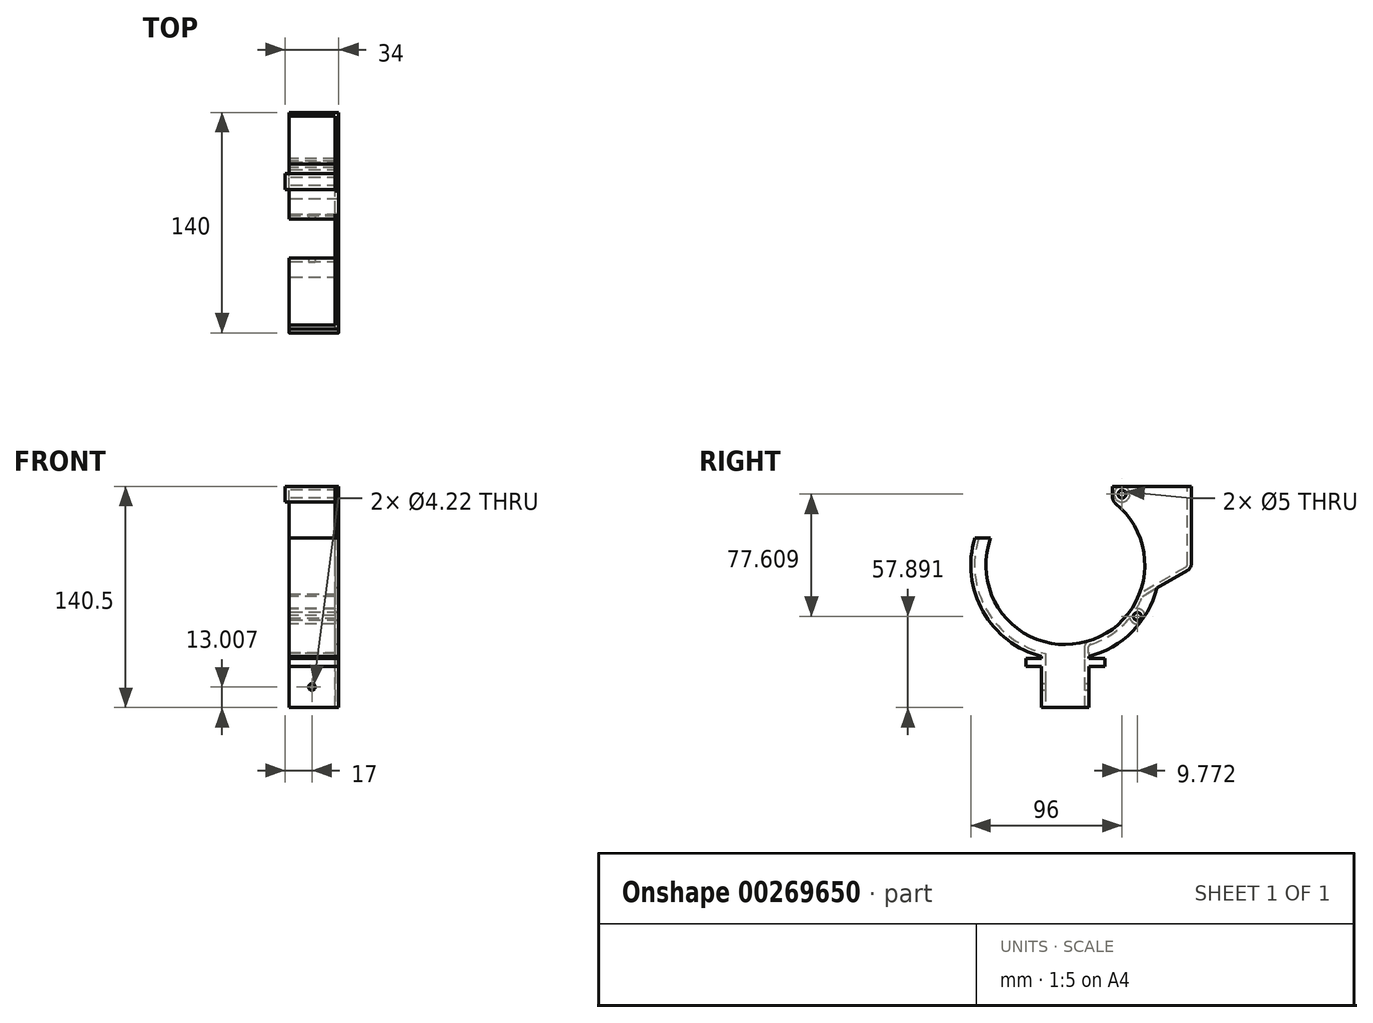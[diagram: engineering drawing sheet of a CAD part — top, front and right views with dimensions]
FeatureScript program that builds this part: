
annotation { "Feature Type Name" : "Feature", "Feature Type Description" : "" }
export const myFeature = defineFeature(function(context is Context, id is Id, definition is map)
    precondition{}
    {
        {
            var Q0;
            Q0=qCreatedBy(makeId("Right.planeOp"),FACE);
            var sketch = newSketch(context, id + "F0", { "sketchPlane" : qUnion([Q0])});
            skLineSegment(sketch, "E0", {"start": v(50, -52.08) * mm, "end": v(50, 0) * mm});
            skLineSegment(sketch, "E1", {"start": v(50, 0) * mm, "end": v(0, 0) * mm});
            skArc(sketch, "E2", {"start": v(-77.52, -32.91) * mm, "mid": v(-15.33, -98.32) * mm, "end": v(0, -9.38) * mm});
            skLineSegment(sketch, "E3", {"start": v(0, 0) * mm, "end": v(0, -9.38) * mm});
            skLineSegment(sketch, "E4", {"start": v(50, -52.08) * mm, "end": v(28.18, -64.68) * mm});
            skCircle(sketch, "E5", {"center": v(-30, -50) * mm, "radius": 50.5 * mm, "construction": true});
            skLineSegment(sketch, "E6", {"start": v(-77.52, -32.91) * mm, "end": v(-87.52, -32.91) * mm});
            skLineSegment(sketch, "E7", {"start": v(-15, -140.5) * mm, "end": v(-15, -108.1) * mm});
            skLineSegment(sketch, "E8", {"start": v(-45, -108.1) * mm, "end": v(-45, -140.5) * mm});
            skLineSegment(sketch, "E9", {"start": v(-45, -140.5) * mm, "end": v(-15, -140.5) * mm});
            skArc(sketch, "E10", {"start": v(-15, -108.1) * mm, "mid": v(12.54, -92.3) * mm, "end": v(28.18, -64.68) * mm});
            skArc(sketch, "E11.trimOffspring", {"start": v(-87.52, -32.91) * mm, "mid": v(-82.23, -79.54) * mm, "end": v(-45, -108.1) * mm});
            skLineSegment(sketch, "E12", {"start": v(-30, -50) * mm, "end": v(-30, -129.79) * mm, "construction": true});
            skSolve(sketch);
        }
        {
            var Q0;
            Q0 = qSketchRegion(id + "F0", true);
            extrude(context, id + "F1", {"entities" : qUnion([Q0]), "depth" : 34 * mm});
        }
        {
            var Q0;
            Q0=makeQuery(id+"F1.opExtrude","SWEPT_EDGE",EDGE,{"disambiguationData":[OSD([sQuery(id+"F0.wireOp",EDGE,"E0"),sQuery(id+"F0.wireOp",EDGE,"E4")])]});
            var Q1;
            Q1=makeQuery(id+"F1.opExtrude","SWEPT_EDGE",EDGE,{"disambiguationData":[OSD([sQuery(id+"F0.wireOp",EDGE,"E2"),sQuery(id+"F0.wireOp",EDGE,"E3")])]});
            fillet(context, id + "F2", {"entities" : qUnion([Q0, Q1]), "radius" : 5 * mm, "tangentPropagation" : true, "allowEdgeOverflow" : false});
        }
        {
            var Q0;
            Q0=makeQuery(id+"F1.opExtrude","SWEPT_FACE",FACE,{"disambiguationData":[OSD([sQuery(id+"F0.wireOp",EDGE,"E1")])]});
            var Q1;
            Q1=makeQuery(id+"F1.opExtrude","SWEPT_FACE",FACE,{"disambiguationData":[OSD([sQuery(id+"F0.wireOp",EDGE,"E2")])]});
            var Q2;
            Q2=makeQuery(id+"F2.opFillet","BLEND_FACE",FACE,{"disambiguationData":[OSD([sQuery(id+"F0.wireOp",EDGE,"E2"),sQuery(id+"F0.wireOp",EDGE,"E3")])]});
            var Q3;
            Q3=makeQuery(id+"F1.opExtrude","SWEPT_FACE",FACE,{"disambiguationData":[OSD([sQuery(id+"F0.wireOp",EDGE,"E3")])]});
            var Q4;
            Q4=makeQuery(id+"F1.opExtrude","SWEPT_FACE",FACE,{"disambiguationData":[OSD([sQuery(id+"F0.wireOp",EDGE,"E6")])]});
            var Q5;
            Q5=makeQuery(id+"F1.opExtrude","SWEPT_FACE",FACE,{"disambiguationData":[OSD([sQuery(id+"F0.wireOp",EDGE,"E9")])]});
            shell(context, id + "F3", {"entities" : qUnion([Q0, Q1, Q2, Q3, Q4, Q5]), "thickness" : 2.4 * mm});
        }
        {
            var Q0;
            Q0=makeQuery(id+"F1.opExtrude","CAP_FACE",FACE,{"disambiguationData":[OSD([sQuery(id+"F0.wireOp",EDGE,"E0"),sQuery(id+"F0.wireOp",EDGE,"E1"),sQuery(id+"F0.wireOp",EDGE,"E2"),sQuery(id+"F0.wireOp",EDGE,"E3"),sQuery(id+"F0.wireOp",EDGE,"E4"),sQuery(id+"F0.wireOp",EDGE,"E6"),sQuery(id+"F0.wireOp",EDGE,"E7"),sQuery(id+"F0.wireOp",EDGE,"E8"),sQuery(id+"F0.wireOp",EDGE,"E9"),sQuery(id+"F0.wireOp",EDGE,"E10"),sQuery(id+"F0.wireOp",EDGE,"E11.trimOffspring")])],"isStart":false});
            var sketch = newSketch(context, id + "F4", { "sketchPlane" : qUnion([Q0])});
            skArc(sketch, "E13.0", {"start": v(-17.9, -99.03) * mm, "mid": v(3.32, -87.94) * mm, "end": v(17.06, -68.32) * mm, "construction": true});
            skArc(sketch, "E14", {"start": v(-17.9, -108.77) * mm, "mid": v(12.64, -92.2) * mm, "end": v(28.89, -61.5) * mm});
            skPoint(sketch, "E15.orphan", {"position": v(1.85, -10.8) * mm});
            skArc(sketch, "E16", {"start": v(-77.52, -32.91) * mm, "mid": v(-47.7, -97.3) * mm, "end": v(17.06, -68.32) * mm});
            skLineSegment(sketch, "E17.0", {"start": v(28.89, -61.5) * mm, "end": v(17.06, -68.32) * mm});
            skPoint(sketch, "E18.orphan", {"position": v(26.09, -63.11) * mm});
            skPoint(sketch, "E19.orphan", {"position": v(-17.4, -106.2) * mm});
            skPoint(sketch, "E20.orphan", {"position": v(46.3, -51.44) * mm});
            skPoint(sketch, "E21.orphan", {"position": v(28.18, -64.68) * mm});
            skPoint(sketch, "E22.orphan", {"position": v(-15, -108.1) * mm});
            skLineSegment(sketch, "E23", {"start": v(-17.9, -99.03) * mm, "end": v(-17.9, -108.77) * mm});
            skSolve(sketch);
        }
        {
            var Q0;
            Q0 = qSketchRegion(id + "F4", true);
            var Q1;
            {var subQ0=sQuery(id+"F0.wireOp",EDGE,"E11.trimOffspring");var subQ1=sQuery(id+"F0.wireOp",EDGE,"E10");var subQ2=sQuery(id+"F0.wireOp",EDGE,"E9");var subQ3=sQuery(id+"F0.wireOp",EDGE,"E8");var subQ4=sQuery(id+"F0.wireOp",EDGE,"E7");var subQ5=sQuery(id+"F0.wireOp",EDGE,"E6");var subQ6=sQuery(id+"F0.wireOp",EDGE,"E4");var subQ7=sQuery(id+"F0.wireOp",EDGE,"E3");var subQ8=sQuery(id+"F0.wireOp",EDGE,"E2");var subQ9=sQuery(id+"F0.wireOp",EDGE,"E1");var subQ10=sQuery(id+"F0.wireOp",EDGE,"E0");Q1=makeQuery(id+"F3.opShell","OFFSET_FACE",FACE,{"disambiguationData":[OSD([subQ10,subQ9,subQ8,subQ7,subQ6,subQ5,subQ4,subQ3,subQ2,subQ1,subQ0]),TDD([makeQuery(id+"F1.opExtrude","CAP_FACE",FACE,{"disambiguationData":[OSD([subQ10,subQ9,subQ8,subQ7,subQ6,subQ5,subQ4,subQ3,subQ2,subQ1,subQ0])],"isStart":true})])]});}
            extrude(context, id + "F5", {"entities" : qUnion([Q0]), "operationType" : NewBodyOperationType.ADD, "endBound" : BoundingType.UP_TO_SURFACE, "oppositeDirection" : true, "endBoundEntityFace" : qUnion([Q1]), "depth" : 25 * mm});
        }
        {
            var Q0;
            Q0=makeQuery(id+"F1.opExtrude","CAP_FACE",FACE,{"disambiguationData":[OSD([sQuery(id+"F0.wireOp",EDGE,"E0"),sQuery(id+"F0.wireOp",EDGE,"E1"),sQuery(id+"F0.wireOp",EDGE,"E2"),sQuery(id+"F0.wireOp",EDGE,"E3"),sQuery(id+"F0.wireOp",EDGE,"E4")])],"isStart":true});
            var sketch = newSketch(context, id + "F6", { "sketchPlane" : qUnion([Q0])});
            skCircle(sketch, "E24", {"center": v(-6, -5) * mm, "radius": 2.5 * mm});
            skCircle(sketch, "E25", {"center": v(-15.77, -82.6) * mm, "radius": 2.5 * mm});
            skArc(sketch, "E26.0", {"start": v(77.52, -32.91) * mm, "mid": v(16.45, -98.65) * mm, "end": v(-1.85, -10.8) * mm, "construction": true});
            skLineSegment(sketch, "E27", {"start": v(30, -50) * mm, "end": v(-6, -5) * mm, "construction": true});
            skLineSegment(sketch, "E28", {"start": v(30, -50) * mm, "end": v(-15.77, -82.6) * mm, "construction": true});
            skLineSegment(sketch, "E29", {"start": v(-6, -5) * mm, "end": v(-15.77, -82.6) * mm, "construction": true});
            skSolve(sketch);
        }
        {
            var Q0;
            Q0 = qSketchRegion(id + "F6", true);
            var Q1;
            Q1=makeQuery(id+"F1.opExtrude","CAP_FACE",FACE,{"disambiguationData":[OSD([sQuery(id+"F0.wireOp",EDGE,"E0"),sQuery(id+"F0.wireOp",EDGE,"E1"),sQuery(id+"F0.wireOp",EDGE,"E2"),sQuery(id+"F0.wireOp",EDGE,"E3"),sQuery(id+"F0.wireOp",EDGE,"E4"),sQuery(id+"F0.wireOp",EDGE,"E6"),sQuery(id+"F0.wireOp",EDGE,"E7"),sQuery(id+"F0.wireOp",EDGE,"E8"),sQuery(id+"F0.wireOp",EDGE,"E9"),sQuery(id+"F0.wireOp",EDGE,"E10"),sQuery(id+"F0.wireOp",EDGE,"E11.trimOffspring")])],"isStart":true});
            extrude(context, id + "F7", {"entities" : qUnion([Q0]), "operationType" : NewBodyOperationType.REMOVE, "endBound" : BoundingType.THROUGH_ALL, "oppositeDirection" : true, "endBoundEntityFace" : qUnion([Q1]), "depth" : 25 * mm});
        }
        {
            var Q0;
            Q0=makeQuery(id+"F5.opExtrude","SWEPT_EDGE",EDGE,{"disambiguationData":[OSD([sQuery(id+"F4.wireOp",EDGE,"E16"),sQuery(id+"F4.wireOp",EDGE,"E23")])]});
            fillet(context, id + "F8", {"entities" : qUnion([Q0]), "radius" : 5 * mm, "tangentPropagation" : true, "allowEdgeOverflow" : false});
        }
        {
            var Q0;
            Q0=makeQuery(id+"F1.opExtrude","SWEPT_FACE",FACE,{"disambiguationData":[OSD([sQuery(id+"F0.wireOp",EDGE,"E10")])]});
            shell(context, id + "F9", {"entities" : qUnion([Q0]), "thickness" : 2.4 * mm});
        }
        {
            var Q0;
            {var subQ0=sQuery(id+"F0.wireOp",EDGE,"E4");var subQ1=sQuery(id+"F0.wireOp",EDGE,"E0");var subQ2=sQuery(id+"F0.wireOp",EDGE,"E3");var subQ3=sQuery(id+"F0.wireOp",EDGE,"E2");var subQ4=sQuery(id+"F0.wireOp",EDGE,"E1");var subQ5=sQuery(id+"F0.wireOp",EDGE,"E11.trimOffspring");var subQ6=sQuery(id+"F0.wireOp",EDGE,"E10");var subQ7=sQuery(id+"F0.wireOp",EDGE,"E9");var subQ8=sQuery(id+"F0.wireOp",EDGE,"E8");var subQ9=sQuery(id+"F0.wireOp",EDGE,"E7");var subQ10=sQuery(id+"F0.wireOp",EDGE,"E6");Q0=makeQuery(id+"F5.boolean.opBoolean","SPLIT",FACE,{"disambiguationData":[TD([makeQuery(id+"F1.opExtrude","SWEPT_FACE",FACE,{"disambiguationData":[OSD([subQ4])]})])],"derivedFrom":makeQuery(id+"F3.opShell","OFFSET_FACE",FACE,{"disambiguationData":[OSD([subQ1,subQ4,subQ3,subQ2,subQ0,subQ10,subQ9,subQ8,subQ7,subQ6,subQ5]),TDD([makeQuery(id+"F1.opExtrude","CAP_FACE",FACE,{"disambiguationData":[OSD([subQ1,subQ4,subQ3,subQ2,subQ0,subQ10,subQ9,subQ8,subQ7,subQ6,subQ5])],"isStart":true})])]})});}
            cPlane(context, id + "F10", {"entities" : qUnion([Q0]), "cplaneType" : CPlaneType.OFFSET, "offset" : 7 * mm, "width" : 150 * mm, "height" : 150 * mm});
        }
        {
            var Q0;
            Q0=qCreatedBy(id+"F10.planeOp",FACE);
            var sketch = newSketch(context, id + "F11", { "sketchPlane" : qUnion([Q0])});
            skLineSegment(sketch, "E30.0", {"start": v(47.6, 0) * mm, "end": v(0, 0) * mm});
            skLineSegment(sketch, "E31.0", {"start": v(47.6, -49.19) * mm, "end": v(47.6, 0) * mm});
            skArc(sketch, "E32.0", {"start": v(47.6, -49.19) * mm, "mid": v(47.25, -50.49) * mm, "end": v(46.3, -51.44) * mm});
            skLineSegment(sketch, "E33.0", {"start": v(46.3, -51.44) * mm, "end": v(17.06, -68.32) * mm});
            skArc(sketch, "E34.0", {"start": v(17.06, -68.32) * mm, "mid": v(18.82, -37.09) * mm, "end": v(1.85, -10.8) * mm});
            skArc(sketch, "E35.0", {"start": v(1.85, -10.8) * mm, "mid": v(0.49, -9.08) * mm, "end": v(0, -6.93) * mm});
            skLineSegment(sketch, "E36.0", {"start": v(0, 0) * mm, "end": v(0, -6.93) * mm});
            skCircle(sketch, "E37.0", {"center": v(6, -5) * mm, "radius": 2.5 * mm});
            skSolve(sketch);
        }
        {
            var Q0;
            Q0 = qSketchRegion(id + "F11", true);
            extrude(context, id + "F12", {"entities" : qUnion([Q0]), "operationType" : NewBodyOperationType.ADD, "depth" : 4 * mm});
        }
        {
            var Q0;
            Q0=makeQuery(id+"F6.imprint","IMPRINT",FACE,{"disambiguationData":[TD([[makeQuery(id+"F6.imprint","IMPRINT",EDGE,{"derivedFrom":sQuery(id+"F6.wireOp",EDGE,"E24")}),-1.0]])]});
            var sketch = newSketch(context, id + "F13", { "sketchPlane" : qUnion([Q0])});
            skCircle(sketch, "E38.0", {"center": v(-6, -5) * mm, "radius": 2.5 * mm});
            skCircle(sketch, "E39", {"center": v(-6, -5) * mm, "radius": 5 * mm});
            skSolve(sketch);
        }
        {
            var Q0;
            Q0 = qSketchRegion(id + "F13", true);
            var Q1;
            {var subQ0=sQuery(id+"F0.wireOp",EDGE,"E4");var subQ1=sQuery(id+"F0.wireOp",EDGE,"E0");var subQ2=sQuery(id+"F0.wireOp",EDGE,"E3");var subQ3=sQuery(id+"F0.wireOp",EDGE,"E2");var subQ4=sQuery(id+"F0.wireOp",EDGE,"E1");var subQ5=sQuery(id+"F0.wireOp",EDGE,"E11.trimOffspring");var subQ6=sQuery(id+"F0.wireOp",EDGE,"E10");var subQ7=sQuery(id+"F0.wireOp",EDGE,"E9");var subQ8=sQuery(id+"F0.wireOp",EDGE,"E8");var subQ9=sQuery(id+"F0.wireOp",EDGE,"E7");var subQ10=sQuery(id+"F0.wireOp",EDGE,"E6");Q1=makeQuery(id+"F5.boolean.opBoolean","SPLIT",FACE,{"disambiguationData":[TD([makeQuery(id+"F1.opExtrude","SWEPT_FACE",FACE,{"disambiguationData":[OSD([subQ4])]})])],"derivedFrom":makeQuery(id+"F3.opShell","OFFSET_FACE",FACE,{"disambiguationData":[OSD([subQ1,subQ4,subQ3,subQ2,subQ0,subQ10,subQ9,subQ8,subQ7,subQ6,subQ5]),TDD([makeQuery(id+"F1.opExtrude","CAP_FACE",FACE,{"disambiguationData":[OSD([subQ1,subQ4,subQ3,subQ2,subQ0,subQ10,subQ9,subQ8,subQ7,subQ6,subQ5])],"isStart":false})])]})});}
            extrude(context, id + "F14", {"entities" : qUnion([Q0]), "operationType" : NewBodyOperationType.ADD, "endBound" : BoundingType.UP_TO_SURFACE, "oppositeDirection" : true, "endBoundEntityFace" : qUnion([Q1]), "depth" : 25 * mm});
        }
        {
            var Q0;
            Q0=makeQuery(id+"F6.imprint","IMPRINT",FACE,{"disambiguationData":[TD([[makeQuery(id+"F6.imprint","IMPRINT",EDGE,{"derivedFrom":sQuery(id+"F6.wireOp",EDGE,"E24")}),-1.0]])]});
            var sketch = newSketch(context, id + "F15", { "sketchPlane" : qUnion([Q0])});
            skLineSegment(sketch, "E40.0", {"start": v(45, -109.49) * mm, "end": v(45, -114.49) * mm});
            skLineSegment(sketch, "E41.0", {"start": v(15, -114.49) * mm, "end": v(15, -109.49) * mm});
            skLineSegment(sketch, "E42.bottom", {"start": v(5, -109.49) * mm, "end": v(15, -109.49) * mm});
            skLineSegment(sketch, "E42.top", {"start": v(5, -114.49) * mm, "end": v(15, -114.49) * mm});
            skLineSegment(sketch, "E42.left", {"start": v(5, -109.49) * mm, "end": v(5, -114.49) * mm});
            skLineSegment(sketch, "E42.right", {"start": v(55, -109.49) * mm, "end": v(55, -114.49) * mm});
            skLineSegment(sketch, "E43.trimOffspring", {"start": v(45, -109.49) * mm, "end": v(55, -109.49) * mm});
            skLineSegment(sketch, "E44.trimOffspring", {"start": v(45, -114.49) * mm, "end": v(55, -114.49) * mm});
            skPoint(sketch, "E45.orphan", {"position": v(15, -140.5) * mm});
            skPoint(sketch, "E46.orphan", {"position": v(45, -140.5) * mm});
            skPoint(sketch, "E47.orphan", {"position": v(45, -108.1) * mm});
            skPoint(sketch, "E48.orphan", {"position": v(15, -108.1) * mm});
            skSolve(sketch);
        }
        {
            var Q0;
            Q0 = qSketchRegion(id + "F15", true);
            var Q1;
            Q1=makeQuery(id+"F1.opExtrude","CAP_FACE",FACE,{"disambiguationData":[OSD([sQuery(id+"F0.wireOp",EDGE,"E0"),sQuery(id+"F0.wireOp",EDGE,"E1"),sQuery(id+"F0.wireOp",EDGE,"E2"),sQuery(id+"F0.wireOp",EDGE,"E3"),sQuery(id+"F0.wireOp",EDGE,"E4"),sQuery(id+"F0.wireOp",EDGE,"E6"),sQuery(id+"F0.wireOp",EDGE,"E7"),sQuery(id+"F0.wireOp",EDGE,"E8"),sQuery(id+"F0.wireOp",EDGE,"E9"),sQuery(id+"F0.wireOp",EDGE,"E10"),sQuery(id+"F0.wireOp",EDGE,"E11.trimOffspring")])],"isStart":false});
            extrude(context, id + "F16", {"entities" : qUnion([Q0]), "operationType" : NewBodyOperationType.ADD, "endBound" : BoundingType.UP_TO_SURFACE, "oppositeDirection" : true, "endBoundEntityFace" : qUnion([Q1]), "depth" : 25 * mm});
        }
        {
            var Q0;
            {var subQ2=sQuery(id+"F0.wireOp",EDGE,"E9");var subQ5=sQuery(id+"F0.wireOp",EDGE,"E8");Q0=makeQuery(id+"F16.boolean.opBoolean","SPLIT",FACE,{"disambiguationData":[TD([makeQuery(id+"F1.opExtrude","SWEPT_FACE",FACE,{"disambiguationData":[OSD([subQ2])]})])],"derivedFrom":makeQuery(id+"F1.opExtrude","SWEPT_FACE",FACE,{"disambiguationData":[OSD([subQ5])]})});}
            var sketch = newSketch(context, id + "F17", { "sketchPlane" : qUnion([Q0])});
            skLineSegment(sketch, "E49", {"start": v(0, -127.5) * mm, "end": v(34, -127.5) * mm, "construction": true});
            skLineSegment(sketch, "E50", {"start": v(17, -140.5) * mm, "end": v(17, -114.49) * mm, "construction": true});
            skCircle(sketch, "E51", {"center": v(17, -127.5) * mm, "radius": 2.1 * mm});
            skSolve(sketch);
        }
        {
            var Q0;
            Q0 = qSketchRegion(id + "F17", true);
            extrude(context, id + "F18", {"entities" : qUnion([Q0]), "operationType" : NewBodyOperationType.REMOVE, "endBound" : BoundingType.THROUGH_ALL, "oppositeDirection" : true, "depth" : 25 * mm});
        }
        {
            var Q0;
            {var subQ0=sQuery(id+"F0.wireOp",EDGE,"E4");var subQ1=sQuery(id+"F0.wireOp",EDGE,"E0");var subQ2=sQuery(id+"F0.wireOp",EDGE,"E3");var subQ3=sQuery(id+"F0.wireOp",EDGE,"E2");var subQ4=sQuery(id+"F0.wireOp",EDGE,"E1");var subQ5=sQuery(id+"F0.wireOp",EDGE,"E11.trimOffspring");var subQ6=sQuery(id+"F0.wireOp",EDGE,"E10");var subQ7=sQuery(id+"F0.wireOp",EDGE,"E9");var subQ8=sQuery(id+"F0.wireOp",EDGE,"E8");var subQ9=sQuery(id+"F0.wireOp",EDGE,"E7");var subQ10=sQuery(id+"F0.wireOp",EDGE,"E6");Q0=makeQuery(id+"F5.boolean.opBoolean","SPLIT",FACE,{"disambiguationData":[TD([makeQuery(id+"F1.opExtrude","SWEPT_FACE",FACE,{"disambiguationData":[OSD([subQ4])]})])],"derivedFrom":makeQuery(id+"F3.opShell","OFFSET_FACE",FACE,{"disambiguationData":[OSD([subQ1,subQ4,subQ3,subQ2,subQ0,subQ10,subQ9,subQ8,subQ7,subQ6,subQ5]),TDD([makeQuery(id+"F1.opExtrude","CAP_FACE",FACE,{"disambiguationData":[OSD([subQ1,subQ4,subQ3,subQ2,subQ0,subQ10,subQ9,subQ8,subQ7,subQ6,subQ5])],"isStart":true})])]})});}
            var sketch = newSketch(context, id + "F19", { "sketchPlane" : qUnion([Q0])});
            skLineSegment(sketch, "E52.bottom", {"start": v(-105.43, 8.57) * mm, "end": v(83.7, 8.57) * mm});
            skLineSegment(sketch, "E52.top", {"start": v(-105.43, -145.94) * mm, "end": v(83.7, -145.94) * mm});
            skLineSegment(sketch, "E52.left", {"start": v(-105.43, 8.57) * mm, "end": v(-105.43, -145.94) * mm});
            skLineSegment(sketch, "E52.right", {"start": v(83.7, 8.57) * mm, "end": v(83.7, -145.94) * mm});
            skCircle(sketch, "E53.0", {"center": v(6, -5) * mm, "radius": 5 * mm});
            skSolve(sketch);
        }
        {
            var Q0;
            Q0 = qSketchRegion(id + "F19", true);
            extrude(context, id + "F20", {"entities" : qUnion([Q0]), "operationType" : NewBodyOperationType.REMOVE, "endBound" : BoundingType.THROUGH_ALL, "oppositeDirection" : true, "depth" : 25 * mm});
        }
        {
            var Q0;
            Q0=makeQuery(id+"F12.opExtrude","CAP_FACE",FACE,{"disambiguationData":[OSD([sQuery(id+"F11.wireOp",EDGE,"E30.0"),sQuery(id+"F11.wireOp",EDGE,"E31.0"),sQuery(id+"F11.wireOp",EDGE,"E32.0"),sQuery(id+"F11.wireOp",EDGE,"E33.0"),sQuery(id+"F11.wireOp",EDGE,"E34.0"),sQuery(id+"F11.wireOp",EDGE,"E35.0"),sQuery(id+"F11.wireOp",EDGE,"E36.0"),sQuery(id+"F11.wireOp",EDGE,"E37.0")])],"isStart":false});
            var sketch = newSketch(context, id + "F21", { "sketchPlane" : qUnion([Q0])});
            skLineSegment(sketch, "E54.0.0", {"start": v(47.6, 0) * mm, "end": v(6, 0) * mm});
            skCircle(sketch, "E54.0.1", {"center": v(6, -5) * mm, "radius": 5 * mm});
            skLineSegment(sketch, "E54.0.2", {"start": v(6, 0) * mm, "end": v(0, 0) * mm});
            skLineSegment(sketch, "E54.0.3", {"start": v(0, 0) * mm, "end": v(0, -6.93) * mm});
            skArc(sketch, "E54.0.4", {"start": v(0, -6.93) * mm, "mid": v(0.49, -9.08) * mm, "end": v(1.85, -10.8) * mm});
            skArc(sketch, "E54.0.5", {"start": v(1.85, -10.8) * mm, "mid": v(18.82, -37.09) * mm, "end": v(17.06, -68.32) * mm});
            skLineSegment(sketch, "E54.0.6", {"start": v(17.06, -68.32) * mm, "end": v(46.3, -51.44) * mm});
            skArc(sketch, "E54.0.7", {"start": v(46.3, -51.44) * mm, "mid": v(47.25, -50.49) * mm, "end": v(47.6, -49.19) * mm});
            skLineSegment(sketch, "E54.0.8", {"start": v(47.6, -49.19) * mm, "end": v(47.6, 0) * mm});
            skSolve(sketch);
        }
        {
            var Q0;
            Q0 = qSketchRegion(id + "F21", true);
            var Q1;
            Q1=makeQuery(id+"F12.opExtrude","CAP_FACE",FACE,{"disambiguationData":[OSD([sQuery(id+"F11.wireOp",EDGE,"E30.0"),sQuery(id+"F11.wireOp",EDGE,"E31.0"),sQuery(id+"F11.wireOp",EDGE,"E32.0"),sQuery(id+"F11.wireOp",EDGE,"E33.0"),sQuery(id+"F11.wireOp",EDGE,"E34.0"),sQuery(id+"F11.wireOp",EDGE,"E35.0"),sQuery(id+"F11.wireOp",EDGE,"E36.0"),sQuery(id+"F11.wireOp",EDGE,"E37.0")])],"isStart":true});
            extrude(context, id + "F22", {"entities" : qUnion([Q0]), "operationType" : NewBodyOperationType.REMOVE, "endBound" : BoundingType.UP_TO_SURFACE, "oppositeDirection" : true, "endBoundEntityFace" : qUnion([Q1]), "depth" : 25 * mm});
        }
        {
            var Q0;
            Q0=makeQuery(id+"F22.boolean.opBoolean","COPY",FACE,{"derivedFrom":makeQuery(id+"F22.opExtrude","CAP_FACE",FACE,{"disambiguationData":[OSD([sQuery(id+"F21.wireOp",EDGE,"E54.0.0"),sQuery(id+"F21.wireOp",EDGE,"E54.0.2"),sQuery(id+"F21.wireOp",EDGE,"E54.0.3"),sQuery(id+"F21.wireOp",EDGE,"E54.0.4"),sQuery(id+"F21.wireOp",EDGE,"E54.0.5"),sQuery(id+"F21.wireOp",EDGE,"E54.0.6"),sQuery(id+"F21.wireOp",EDGE,"E54.0.7"),sQuery(id+"F21.wireOp",EDGE,"E54.0.8")])],"isStart":true})});
            var sketch = newSketch(context, id + "F23", { "sketchPlane" : qUnion([Q0])});
            skCircle(sketch, "E55.0", {"center": v(-6, -5) * mm, "radius": 5 * mm});
            skCircle(sketch, "E56.0", {"center": v(-6, -5) * mm, "radius": 2.5 * mm});
            skSolve(sketch);
        }
        {
            var Q0;
            Q0 = qSketchRegion(id + "F23", true);
            extrude(context, id + "F24", {"entities" : qUnion([Q0]), "operationType" : NewBodyOperationType.ADD, "endBound" : BoundingType.UP_TO_NEXT, "depth" : 25 * mm});
        }
    });
